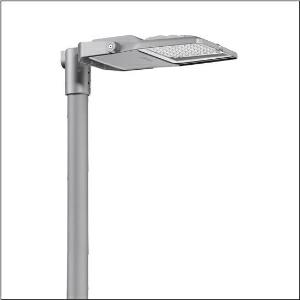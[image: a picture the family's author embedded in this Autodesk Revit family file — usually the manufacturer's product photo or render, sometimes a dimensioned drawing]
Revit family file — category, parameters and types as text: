
# Revit family: floodlight_fl_21_mini___pl33t_5xa7775c2f3a_8bfe
name_source: partatom
category: Lighting Fixtures
units: mm (PartAtom-declared; Revit-internal decimal feet)

## family parameters
Cut with Voids When Loaded = No
Host = Face
Light Source = No
Part Type = Normal
Room Calculation Point = No
Round Connector Dimension = Use Diameter
Shared = No

## types (1)
- --- (1 x LED, 12050 lm, 89 W, 3000K)
    Apparent Load = 89 VA
    CIE Flux Codes = 26 75 99 100 100
    Color Rendering = 70
    Color Temperature = 3000K
    Default Elevation = 1800 mm
    Description = Floodlight FL 21 mini, floodlight, primary light control with lens, of PMMA, primary optical cover: protective disc, of toughened safety glass, transparent, light distribution: PL33T, light emission: direct distribution, installation type: surface-mounted, LED, High Power LED, rated luminous flux: 12.050lm, luminous efficacy: 135lm/W, light colour: 730, colour temperature: 3000K, control gear: Smart Interface (Zhaga), control: flexible luminous flux parameterisation, time-dependent luminous flux control, constant luminous flux control, overheat protection, pre-setting: logarithmic dimming characteristic, with terminal, 6-pole, mains connection: 220..240V, AC, 50/60Hz, start of lifetime: 89W, end of service life: 94W, reduction: 43W, luminaire housing, of diecast aluminium, powder-coated, SITECO metallic grey (DB 702S), corrosivity category C5 mid according to DIN EN ISO 12944, suitable for swimming pools, chlorine-resistant, sealing non-destructively replaceable, please order mast flange separately, mast bracket, of steel, galvanised, powder-coated, SITECO metallic grey (DB 702S), Smart Interface above, protection rating (complete): IP66, insulation class (complete): insulation class II (safety insulation), certification: CE, ENEC, VDE, protection symbol: D, impact resistance: IK08, permissible operating ambient temperature: -40..+40°C, permissible operating ambient temperature for outdoor applications: -40..+50°C, standard: DIN EN 12944, LABS conformity tested according to VDMA 24364:2018-05, packaging unit: 1 piece

Light Distribution: PL33T
    Height = 70 mm
    Lamp = 1 x LED
    Lamp Light Flux = 12050 lm
    Lamp Power = 89 W
    Lamp count = 1
    Length = 485 mm
    Luminous efficacy = 135 lm/W
    Manufacturer = Siteco
    ModVariant = No
    Model = 5XA7775C2F3A
    Mounting Place = Pole
    Mounting Type = Pole annexe
    Number of Poles = 1
    OnlyDefault = Yes
    Power Factor = 1
    Product Name = Floodlight FL 21 mini | PL33T
    Product group = floodlight | pylon annexe
    ProductGroupID = 6201
    Protection Class = Protection class II
    Protection Degree = IP 66
    RLX_Detail_Level = 1
    RLX_Emergency_Light_Flux = 0 lm
    RLX_Emergency_Type = 0
    RLX_Emergency_Type_DB = No
    RlxData = <blob elided: 101037 chars, md5=bbea62a4>
    Socket = socket
    Standby Power = 0 W
    System Light Flux = 12050 lm
    System Power = 89 W
    Type Comments = factory setting: luminous flux: 100 % | dim-lin: 254 | 456 mA
    Type Image = l_1007125.jpg
    URL = http://relux.com
    VarID = @adj_149589
    Voltage = 0 V
    Weight = 0.00 kg
    Width = 337 mm

## geometry (parser evidence)
native form markers: Blend x4, Sweep x13
no freeform markers — native parametric forms only
